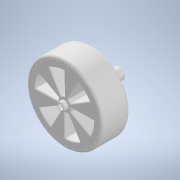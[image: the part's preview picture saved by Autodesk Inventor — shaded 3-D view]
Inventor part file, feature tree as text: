
AUTODESK INVENTOR PART (.ipt)
format: ipt  version: 2021 (Build 250183000, 183)  size: 301,056 bytes
history: native  units: mm
features: sketch x7, extrude x6, fillet x3, pattern_circular x1, hole x1
ambient origin geometry x8: Origin, YZ Plane, XZ Plane, XY Plane, X Axis, Y Axis, Z Axis, Center Point
bodies: Solid1 (feature_tree)
feature tree (18):
  extrude  "Extrusion1"  Depth=20.0mm TaperAngle=0.0deg
  fillet  "Fillet1"  Radius=2.0mm
  extrude  "Extrusion2"  Depth=10.0mm
  fillet  "Fillet2"  [1 undecoded]
  pattern_circular  "Circular Pattern1"  Count=6 Angle=360.0deg
  extrude  "Extrusion3"  Depth=3.0mm TaperAngle=0.0deg
  fillet  "Fillet3"  Radius=1.0mm
  hole  "Hole1"  [1 undecoded]
  extrude  "Extrusion4"  Depth=220.0mm TaperAngle=0.0deg
  extrude  "Extrusion5"  [1 undecoded]
  extrude  "Extrusion6"  [1 undecoded]
  sketch  "Sketch1"  dims[d0=55.0mm d1=20.0mm d2=0.0mm d3=2.0mm]
  sketch  "Sketch2"  dims[d4=42.0mm d5=10.0mm d6=30.0deg]
  sketch  "Sketch3"  dims[d7=0.0mm d8=0.0mm]
  sketch  "Sketch4"  dims[d9=1.0mm d10=60.0mm d11=360.0deg]
  sketch  "Sketch5"  dims[d13=6.0mm d14=3.0mm d15=0.0mm d16=1.0mm]
  sketch  "Sketch6"  dims[d17=4.0mm d18=6.0mm d19=4.0mm d20=2.0mm d21=90.0deg d22=8.0mm d23=20.594885mm d24=260.0mm d25=0.0mm]
  sketch  "Sketch7"  dims[d26=260.0mm d27=0.0mm d28=220.0mm d29=0.0mm]
note: 4 required parameter values undecoded (feature->parameter linkage not recoverable at this tier; creation-order binding heuristic only, values carry confidence <= 0.55)
